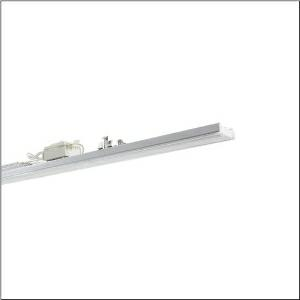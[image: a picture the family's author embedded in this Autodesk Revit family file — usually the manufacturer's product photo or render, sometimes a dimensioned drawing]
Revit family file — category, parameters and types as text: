
# Revit family: licross_21_recessed_mo_52tl12dn4axg
name_source: partatom
category: Lighting Fixtures
units: mm (PartAtom-declared; Revit-internal decimal feet)

## family parameters
Cut with Voids When Loaded = No
Host = Face
Light Source = No
Part Type = Normal
Room Calculation Point = No
Round Connector Dimension = Use Diameter
Shared = No

## types (1)
- --- (1 x LED, 10280 lm, 58 W, 4000K)
    Apparent Load = 58 VA
    CIE Flux Codes = 72 92 99 100 100
    Color Rendering = 80
    Color Temperature = 4000K
    Default Elevation = 1800 mm
    Description = Licross 21 Recessed MO, luminaire insert, of sheet steel, galvanised, coil coated, white, length: 1.500mm, width: 66mm, height: 67mm, LED rated luminous flux: 10.280lm, light colour: 840, SDCM (Standard Deviation of Colour Matching)MacAdam ≤ 3 SDCM (initial), control gear: DALI 2, with plug, 5-pole, with phase selection, mains connection: 220..240V, AC, 50/60Hz, rated input power: 58W, internal wiring halogen-free, primary optical cover: cover, of PMMA, light emission: direct distribution, primary light characteristic: symmetric, protection rating (complete): IP40, insulation class (complete): insulation class I (protective earthing), certification: CE, ENEC, VDE, UKCA, protection symbol: D if used in an environment without relevant dust loads with corresponding accessories, impact resistance: IK06, permissible ambient temperature for indoor applications: -25..+35°C, corresponds to IFS (International Featured Standards) requirements for safety and quality in the food industry, reducing of maximum allowable ambient temperature of 5°C with ceiling mounting, LABS conformity tested according to VDMA 24364:2018-05, The light source and the operating device comply with the requirements of the Ecodesign Regulation (EU) 2019/2020 and are replaceable in accordance with this regulation, packaging unit: 1 piece
    Height = 58 mm
    Lamp = 1 x LED
    Lamp Light Flux = 10280 lm
    Lamp Power = 58 W
    Lamp count = 1
    Length = 1500 mm
    Luminous efficacy = 177 lm/W
    Manufacturer = Siteco
    ModVariant = No
    Model = 52TL12DN4AXG
    Mounting Place = Ceiling
    Mounting Type = Pendant
    Number of Poles = 1
    OnlyDefault = Yes
    Power Factor = 1
    Product Name = Licross 21 Recessed MO
    Product group = luminaire insert | ceiling pendant
    ProductGroupID = 901
    Protection Class = Protection class I
    Protection Degree = IP 40
    RLX_Detail_Level = 1
    RLX_Emergency_Light_Flux = 0 lm
    RLX_Emergency_Type = 0
    RLX_Emergency_Type_DB = No
    RlxData = <blob elided: 24913 chars, md5=f4aa8fa7>
    Socket = socket
    Standby Power = 0 W
    System Light Flux = 10280 lm
    System Power = 58 W
    Type Comments = factory setting: luminous flux: 100 % | dim-lin: 254 | 390 mA
    Type Image = l_1296930.jpg
    URL = http://relux.com
    VarID = @adj_126495
    Voltage = 0 V
    Weight = 0.00 kg
    Width = 66 mm

## geometry (parser evidence)
native form markers: Blend x4, Sweep x11
no freeform markers — native parametric forms only
